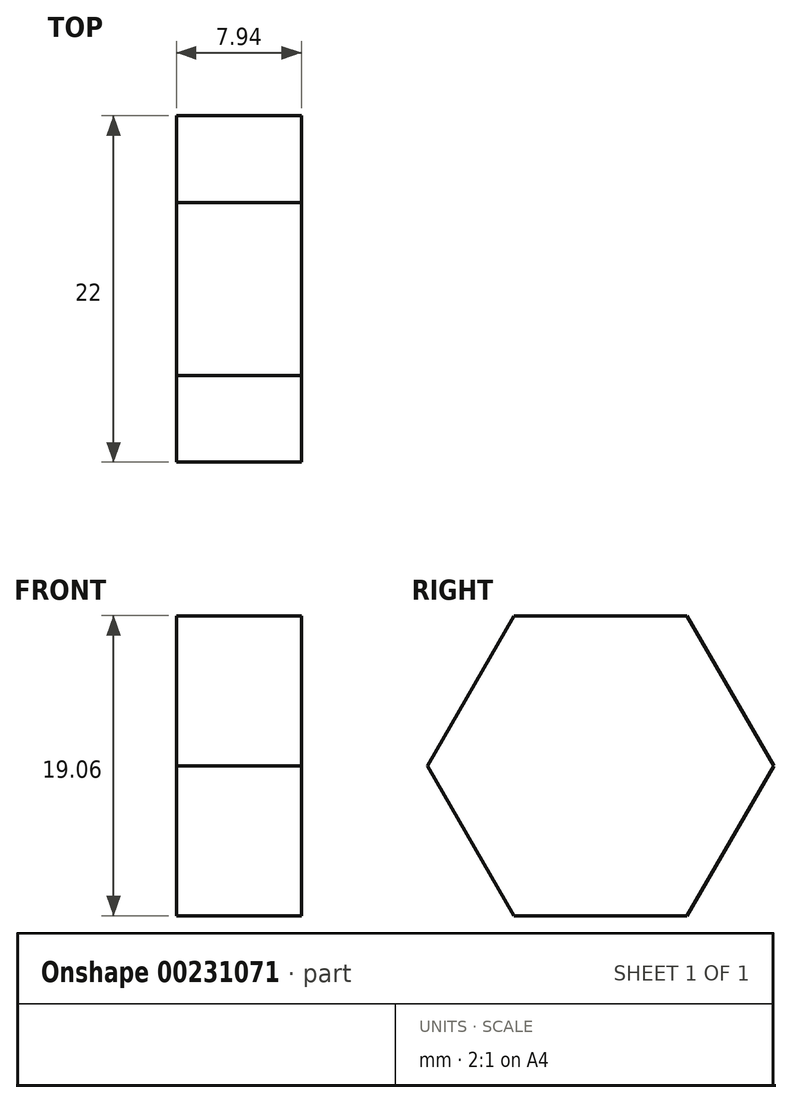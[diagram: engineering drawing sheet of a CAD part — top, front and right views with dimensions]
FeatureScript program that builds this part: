
annotation { "Feature Type Name" : "Feature", "Feature Type Description" : "" }
export const myFeature = defineFeature(function(context is Context, id is Id, definition is map)
    precondition{}
    {
        {
            var Q0;
            Q0=qCreatedBy(makeId("Right.planeOp"),FACE);
            var sketch = newSketch(context, id + "F0", { "sketchPlane" : qUnion([Q0])});
            skCircle(sketch, "E0.cCircle", {"center": v(0, 0) * mm, "radius": 9.53 * mm, "construction": true});
            skLineSegment(sketch, "E0.0", {"start": v(-5.5, 9.53) * mm, "end": v(5.5, 9.53) * mm});
            skLineSegment(sketch, "E0.1", {"start": v(5.5, 9.53) * mm, "end": v(11, 0) * mm});
            skLineSegment(sketch, "E0.2", {"start": v(11, 0) * mm, "end": v(5.5, -9.52) * mm});
            skLineSegment(sketch, "E0.3", {"start": v(5.5, -9.52) * mm, "end": v(-5.5, -9.53) * mm});
            skLineSegment(sketch, "E0.4", {"start": v(-5.5, -9.53) * mm, "end": v(-11, 0) * mm});
            skLineSegment(sketch, "E0.5", {"start": v(-11, 0) * mm, "end": v(-5.5, 9.53) * mm});
            skPoint(sketch, "E0.0.midPoint", {"position": v(0, 9.53) * mm});
            skSolve(sketch);
        }
        {
            var Q0;
            Q0=qSketchRegion(id+"F0",true);
            extrude(context, id + "F1", {"entities" : qUnion([Q0]), "depth" : 7.94 * mm});
        }
    });
